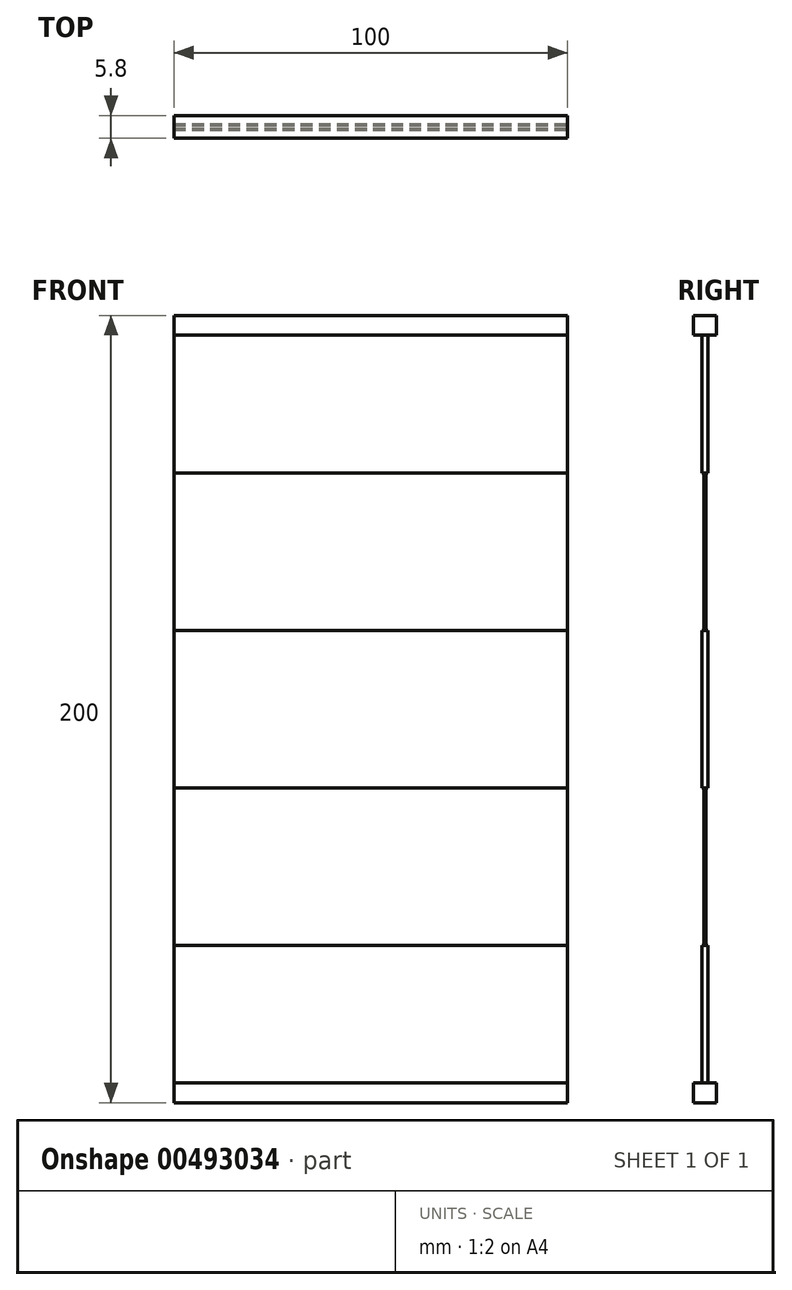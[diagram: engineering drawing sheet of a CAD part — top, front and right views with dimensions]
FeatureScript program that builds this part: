
annotation { "Feature Type Name" : "Feature", "Feature Type Description" : "" }
export const myFeature = defineFeature(function(context is Context, id is Id, definition is map)
    precondition{}
    {
        {
            var Q0;
            Q0=qCreatedBy(makeId("Front.planeOp"),FACE);
            var sketch = newSketch(context, id + "F0", { "sketchPlane" : qUnion([Q0])});
            skLineSegment(sketch, "E0.bottom", {"start": v(50, -100) * mm, "end": v(-50, -100) * mm});
            skLineSegment(sketch, "E0.top", {"start": v(50, 100) * mm, "end": v(-50, 100) * mm});
            skLineSegment(sketch, "E0.left", {"start": v(50, -100) * mm, "end": v(50, 100) * mm});
            skLineSegment(sketch, "E0.right", {"start": v(-50, -100) * mm, "end": v(-50, 100) * mm});
            skPoint(sketch, "E0.middle", {"position": v(0, 0) * mm});
            skLineSegment(sketch, "E1", {"start": v(-50, 60) * mm, "end": v(50, 60) * mm});
            skLineSegment(sketch, "E2", {"start": v(-50, 20) * mm, "end": v(50, 20) * mm});
            skLineSegment(sketch, "E3", {"start": v(-50, -20) * mm, "end": v(50, -20) * mm});
            skLineSegment(sketch, "E4", {"start": v(-50, -60) * mm, "end": v(50, -60) * mm});
            skLineSegment(sketch, "E5", {"start": v(-50, 95) * mm, "end": v(50, 95) * mm});
            skLineSegment(sketch, "E6", {"start": v(-50, -95) * mm, "end": v(50, -95) * mm});
            skSolve(sketch);
        }
        {
            var Q0;
            {var subQ0=sQuery(id+"F0.wireOp",EDGE,"E0.top");Q0=makeQuery(id+"F0.imprint","IMPRINT",FACE,{"disambiguationData":[TD([[makeQuery(id+"F0.imprint","IMPRINT",EDGE,{"derivedFrom":subQ0}),1.0]])]});}
            var Q1;
            {var subQ0=sQuery(id+"F0.wireOp",EDGE,"E0.bottom");Q1=makeQuery(id+"F0.imprint","IMPRINT",FACE,{"disambiguationData":[TD([[makeQuery(id+"F0.imprint","IMPRINT",EDGE,{"derivedFrom":subQ0}),-1.0]])]});}
            extrude(context, id + "F1", {"entities" : qUnion([Q0, Q1]), "endBound" : BoundingType.SYMMETRIC, "depth" : 5.8 * mm, "offsetDistance" : 25 * mm});
        }
        {
            var Q0;
            {var subQ0=sQuery(id+"F0.wireOp",EDGE,"E1");Q0=makeQuery(id+"F0.imprint","IMPRINT",FACE,{"disambiguationData":[TD([[makeQuery(id+"F0.imprint","IMPRINT",EDGE,{"derivedFrom":subQ0}),1.0]])]});}
            var Q1;
            {var subQ0=sQuery(id+"F0.wireOp",EDGE,"E2");Q1=makeQuery(id+"F0.imprint","IMPRINT",FACE,{"disambiguationData":[TD([[makeQuery(id+"F0.imprint","IMPRINT",EDGE,{"derivedFrom":subQ0}),-1.0]])]});}
            var Q2;
            {var subQ0=sQuery(id+"F0.wireOp",EDGE,"E4");Q2=makeQuery(id+"F0.imprint","IMPRINT",FACE,{"disambiguationData":[TD([[makeQuery(id+"F0.imprint","IMPRINT",EDGE,{"derivedFrom":subQ0}),-1.0]])]});}
            extrude(context, id + "F2", {"entities" : qUnion([Q0, Q1, Q2]), "endBound" : BoundingType.SYMMETRIC, "depth" : 1.6 * mm, "offsetDistance" : 25 * mm});
        }
        {
            var Q0;
            {var subQ0=sQuery(id+"F0.wireOp",EDGE,"E1");Q0=makeQuery(id+"F0.imprint","IMPRINT",FACE,{"disambiguationData":[TD([[makeQuery(id+"F0.imprint","IMPRINT",EDGE,{"derivedFrom":subQ0}),-1.0]])]});}
            var Q1;
            {var subQ0=sQuery(id+"F0.wireOp",EDGE,"E3");Q1=makeQuery(id+"F0.imprint","IMPRINT",FACE,{"disambiguationData":[TD([[makeQuery(id+"F0.imprint","IMPRINT",EDGE,{"derivedFrom":subQ0}),-1.0]])]});}
            extrude(context, id + "F3", {"entities" : qUnion([Q0, Q1]), "endBound" : BoundingType.SYMMETRIC, "depth" : 0.6 * mm, "offsetDistance" : 25 * mm});
        }
    });
